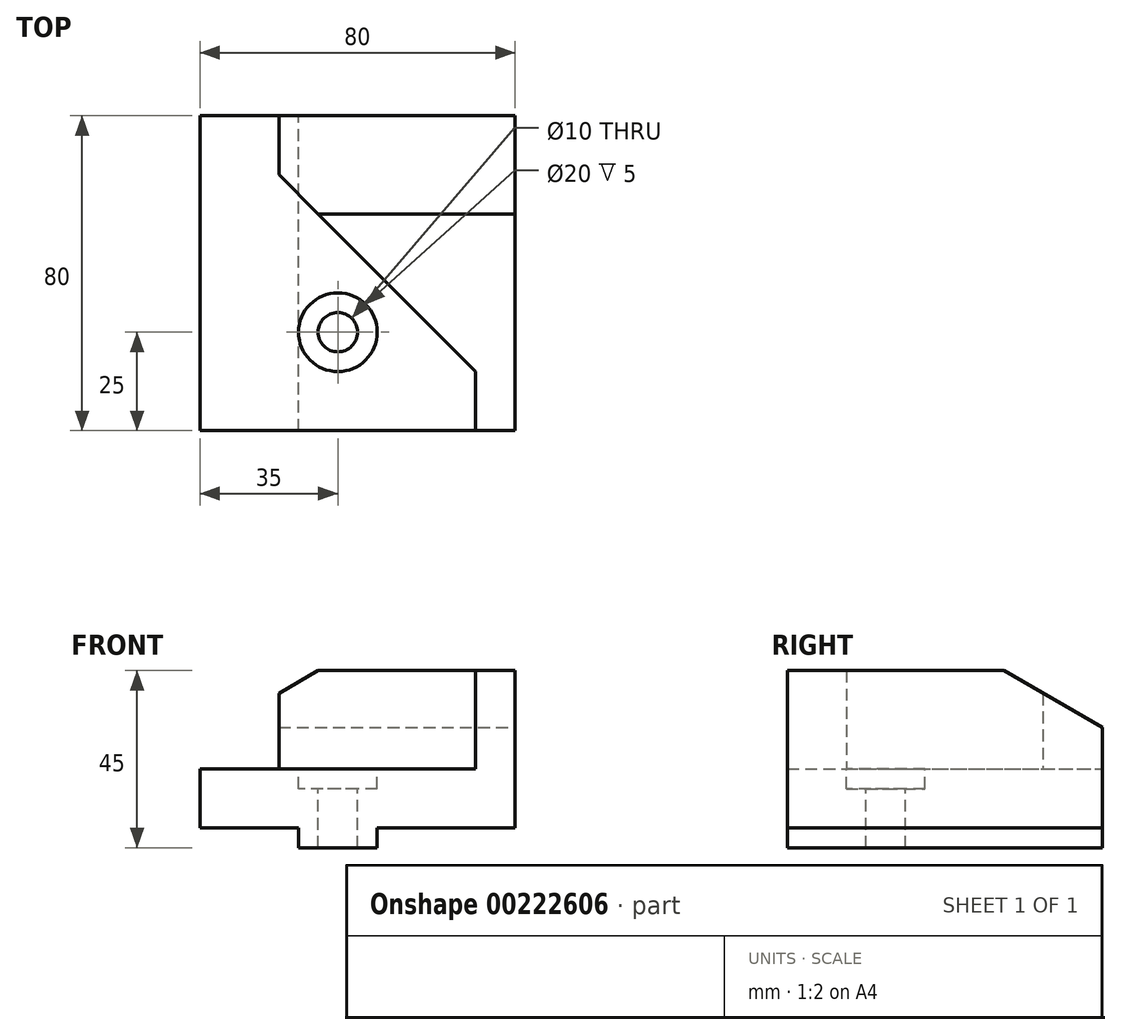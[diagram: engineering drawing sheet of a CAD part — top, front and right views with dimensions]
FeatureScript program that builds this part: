
annotation { "Feature Type Name" : "Feature", "Feature Type Description" : "" }
export const myFeature = defineFeature(function(context is Context, id is Id, definition is map)
    precondition{}
    {
        {
            var Q0;
            Q0=qCreatedBy(makeId("Front.planeOp"),FACE);
            var sketch = newSketch(context, id + "F0", { "sketchPlane" : qUnion([Q0])});
            skLineSegment(sketch, "E0", {"start": v(30, 25) * mm, "end": v(30, 0) * mm});
            skLineSegment(sketch, "E1", {"start": v(30, 0) * mm, "end": v(-40, 0) * mm});
            skLineSegment(sketch, "E2", {"start": v(-40, 0) * mm, "end": v(-40, -15) * mm});
            skLineSegment(sketch, "E3", {"start": v(-40, -15) * mm, "end": v(-15, -15) * mm});
            skLineSegment(sketch, "E4", {"start": v(-15, -15) * mm, "end": v(-15, -20) * mm});
            skLineSegment(sketch, "E5", {"start": v(-15, -20) * mm, "end": v(5, -20) * mm});
            skLineSegment(sketch, "E6", {"start": v(5, -20) * mm, "end": v(5, -15) * mm});
            skLineSegment(sketch, "E7", {"start": v(5, -15) * mm, "end": v(40, -15) * mm});
            skLineSegment(sketch, "E8", {"start": v(40, -15) * mm, "end": v(40, 25) * mm});
            skLineSegment(sketch, "E9", {"start": v(40, 25) * mm, "end": v(30, 25) * mm});
            skSolve(sketch);
        }
        {
            var Q0;
            Q0=makeQuery(id+"F0.imprint","IMPRINT",FACE,{"disambiguationData":[TD([[makeQuery(id+"F0.imprint","IMPRINT",EDGE,{"derivedFrom":sQuery(id+"F0.wireOp",EDGE,"E0")}),1.0]])]});
            extrude(context, id + "F1", {"entities" : qUnion([Q0]), "endBound" : BoundingType.SYMMETRIC, "depth" : 80 * mm});
        }
        {
            var Q0;
            Q0=makeQuery(id+"F1.opExtrude","SWEPT_FACE",FACE,{"disambiguationData":[OSD([sQuery(id+"F0.wireOp",EDGE,"E1")])]});
            var sketch = newSketch(context, id + "F2", { "sketchPlane" : qUnion([Q0])});
            skLineSegment(sketch, "E10", {"start": v(30, 40) * mm, "end": v(-20, 40) * mm});
            skLineSegment(sketch, "E11", {"start": v(30, -25) * mm, "end": v(30, 40) * mm});
            skLineSegment(sketch, "E12", {"start": v(30, -25) * mm, "end": v(-20, 25) * mm});
            skLineSegment(sketch, "E13", {"start": v(-20, 25) * mm, "end": v(-20, 40) * mm});
            skSolve(sketch);
        }
        {
            var Q0;
            Q0=makeQuery(id+"F2.imprint","IMPRINT",FACE,{"disambiguationData":[TD([[makeQuery(id+"F2.imprint","IMPRINT",EDGE,{"derivedFrom":sQuery(id+"F2.wireOp",EDGE,"E10")}),1.0]])]});
            var Q1;
            Q1=makeQuery(id+"F1.opExtrude","SWEPT_FACE",FACE,{"disambiguationData":[OSD([sQuery(id+"F0.wireOp",EDGE,"E9")])]});
            extrude(context, id + "F3", {"entities" : qUnion([Q0]), "operationType" : NewBodyOperationType.ADD, "endBound" : BoundingType.UP_TO_SURFACE, "endBoundEntityFace" : qUnion([Q1]), "depth" : 25 * mm});
        }
        {
            var Q0;
            Q0=makeQuery(id+"F1.opExtrude","SWEPT_FACE",FACE,{"disambiguationData":[OSD([sQuery(id+"F0.wireOp",EDGE,"E8")])]});
            var sketch = newSketch(context, id + "F4", { "sketchPlane" : qUnion([Q0])});
            skLineSegment(sketch, "E14", {"start": v(15, 25) * mm, "end": v(40, 10.57) * mm});
            skLineSegment(sketch, "E15", {"start": v(40, 10.57) * mm, "end": v(40, 25) * mm});
            skLineSegment(sketch, "E16", {"start": v(40, 25) * mm, "end": v(15, 25) * mm});
            skSolve(sketch);
        }
        {
            var Q0;
            Q0=makeQuery(id+"F4.imprint","IMPRINT",FACE,{"disambiguationData":[TD([[makeQuery(id+"F4.imprint","IMPRINT",EDGE,{"derivedFrom":sQuery(id+"F4.wireOp",EDGE,"E14")}),1.0]])]});
            var Q1;
            Q1=makeQuery(id+"F3.opExtrude","SWEPT_FACE",FACE,{"disambiguationData":[OSD([sQuery(id+"F2.wireOp",EDGE,"E13")])]});
            extrude(context, id + "F5", {"entities" : qUnion([Q0]), "operationType" : NewBodyOperationType.REMOVE, "endBound" : BoundingType.UP_TO_NEXT, "oppositeDirection" : true, "endBoundEntityFace" : qUnion([Q1]), "depth" : 59.5 * mm});
        }
        {
            var Q0;
            Q0=qCreatedBy(makeId("Top.planeOp"),FACE);
            var sketch = newSketch(context, id + "F6", { "sketchPlane" : qUnion([Q0])});
            skPoint(sketch, "E17", {"position": v(-5, -15) * mm});
            skSolve(sketch);
        }
        {
            var Q0;
            Q0=sQuery(id+"F6.wireOp",VERTEX,"E17");
            var Q1;
            Q1=makeQuery(id+"F1.opExtrude","SWEPT_BODY",BODY,{"disambiguationData":[OSD([sQuery(id+"F0.wireOp",EDGE,"E0"),sQuery(id+"F0.wireOp",EDGE,"E1"),sQuery(id+"F0.wireOp",EDGE,"E2"),sQuery(id+"F0.wireOp",EDGE,"E3"),sQuery(id+"F0.wireOp",EDGE,"E4"),sQuery(id+"F0.wireOp",EDGE,"E5"),sQuery(id+"F0.wireOp",EDGE,"E6"),sQuery(id+"F0.wireOp",EDGE,"E7"),sQuery(id+"F0.wireOp",EDGE,"E8"),sQuery(id+"F0.wireOp",EDGE,"E9")])]});
            hole(context, id + "F7", {"style" : HoleStyle.C_BORE, "endStyle" : HoleEndStyle.THROUGH, "holeDiameter" : 10 * mm, "cBoreDiameter" : 20 * mm, "cBoreDepth" : 5 * mm, "locations" : qUnion([Q0]), "scope" : qUnion([Q1]), "isTappedThrough" : true});
        }
    });
